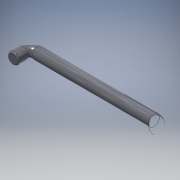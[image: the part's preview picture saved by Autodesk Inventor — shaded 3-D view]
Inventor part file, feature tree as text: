
AUTODESK INVENTOR PART (.ipt)
format: ipt  version: 2016 (Build 200138000, 138)  size: 139,264 bytes
history: native  units: mm
features: sketch x2, plane x1, sweep x1, fillet x1
ambient origin geometry x8: Origin, YZ Plane, XZ Plane, XY Plane, X Axis, Y Axis, Z Axis, Center Point
bodies: Body1 (feature_tree)
feature tree (5):
  sketch  "Sketch2"  dims[d11=52.5mm d12=7.0mm d13=3.0mm]
  plane  "Work Plane1"
  sweep  "Sweep1"
  fillet  "Fillet1"  Radius=3.0mm
  sketch  "Sketch3"  dims[d14=4.5mm d15=0.0mm d16=0.0mm d17=0.5mm]
